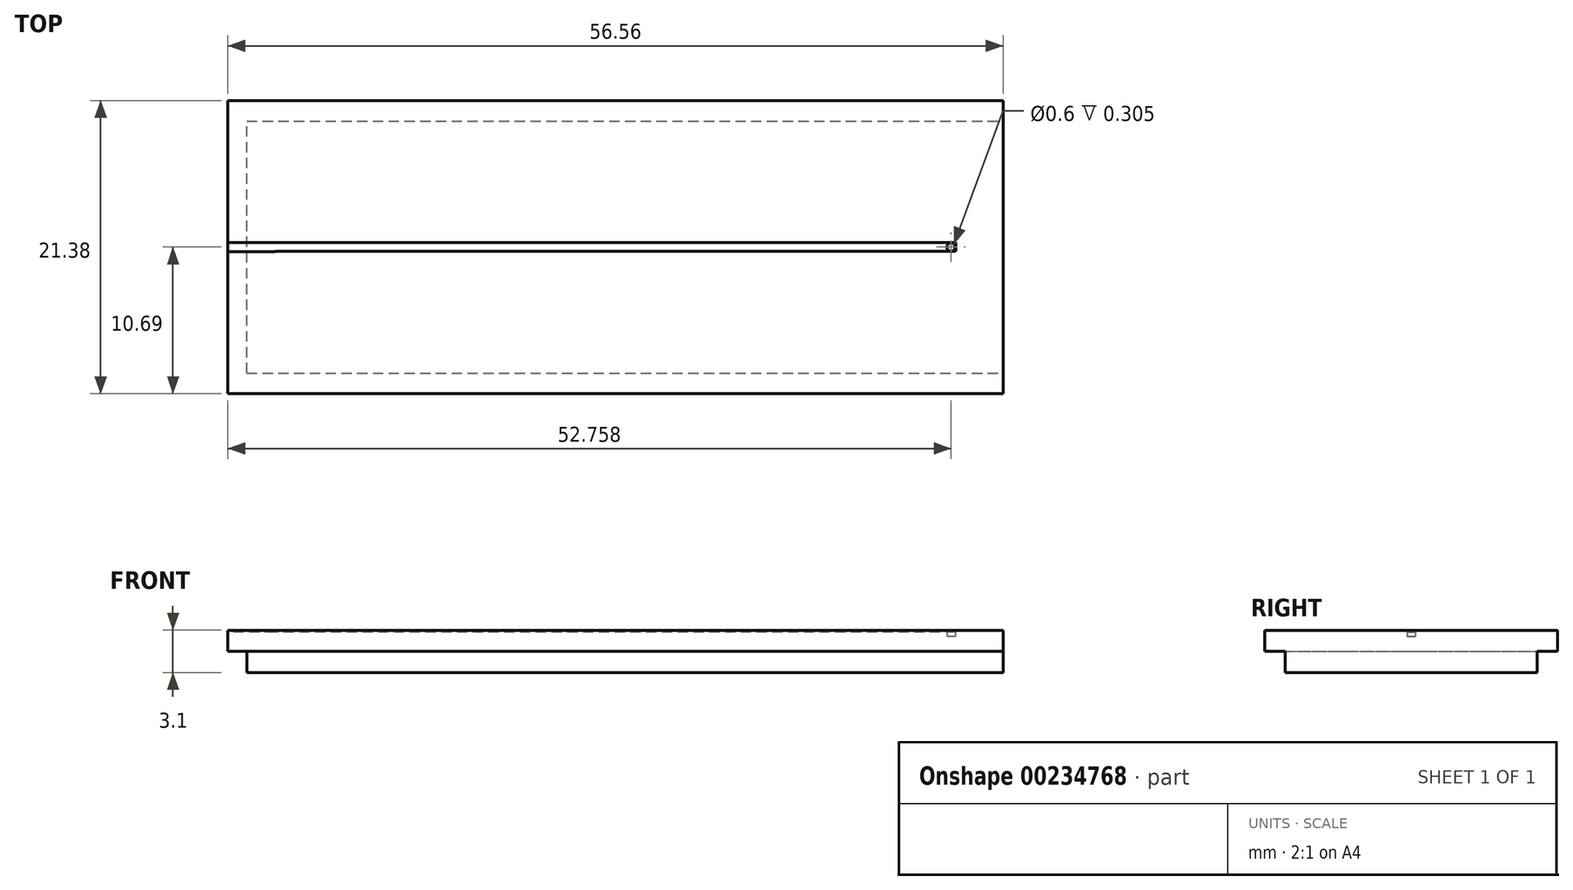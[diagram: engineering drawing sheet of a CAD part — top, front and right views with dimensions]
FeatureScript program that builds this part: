
annotation { "Feature Type Name" : "Feature", "Feature Type Description" : "" }
export const myFeature = defineFeature(function(context is Context, id is Id, definition is map)
    precondition{}
    {
        {
            var Q0;
            Q0=qCreatedBy(makeId("Top.planeOp"),FACE);
            var sketch = newSketch(context, id + "F5", { "sketchPlane" : qUnion([Q0])});
            skLineSegment(sketch, "E0.bottom", {"start": v(28.28, -10.69) * mm, "end": v(-28.28, -10.69) * mm});
            skLineSegment(sketch, "E0.top", {"start": v(28.28, 10.69) * mm, "end": v(-28.28, 10.69) * mm});
            skLineSegment(sketch, "E0.left", {"start": v(28.28, -10.69) * mm, "end": v(28.28, 10.69) * mm});
            skLineSegment(sketch, "E0.right", {"start": v(-28.28, -10.69) * mm, "end": v(-28.28, 10.69) * mm});
            skSolve(sketch);
        }
        {
            var Q0;
            Q0=makeQuery(id+"F5.imprint","IMPRINT",FACE,{"disambiguationData":[TD([[makeQuery(id+"F5.imprint","IMPRINT",EDGE,{"derivedFrom":sQuery(id+"F5.wireOp",EDGE,"E0.bottom")}),-1.0]])]});
            var sketch = newSketch(context, id + "F6", { "sketchPlane" : qUnion([Q0])});
            skCircle(sketch, "E1", {"center": v(24.48, 0) * mm, "radius": 0.3 * mm});
            skSolve(sketch);
        }
        {
            var Q0;
            Q0=makeQuery(id+"F6.imprint","IMPRINT",FACE,{"disambiguationData":[TD([[makeQuery(id+"F6.imprint","IMPRINT",EDGE,{"derivedFrom":sQuery(id+"F6.wireOp",EDGE,"E1")}),-1.0]])]});
            extrude(context, id + "F7", {"entities" : qUnion([Q0]), "depth" : 0.3 * mm});
        }
        {
            var Q0;
            Q0=makeQuery(id+"F7.opExtrude","CAP_FACE",FACE,{"disambiguationData":[OSD([sQuery(id+"F5.wireOp",EDGE,"E0.bottom"),sQuery(id+"F5.wireOp",EDGE,"E0.top"),sQuery(id+"F5.wireOp",EDGE,"E0.left"),sQuery(id+"F5.wireOp",EDGE,"E0.right"),sQuery(id+"F6.wireOp",EDGE,"E1")])],"isStart":false});
            var sketch = newSketch(context, id + "F0", { "sketchPlane" : qUnion([Q0])});
            skLineSegment(sketch, "E2.bottom", {"start": v(24.83, -0.32) * mm, "end": v(-24.83, -0.32) * mm});
            skLineSegment(sketch, "E2.top", {"start": v(24.83, 0.32) * mm, "end": v(-24.83, 0.32) * mm});
            skLineSegment(sketch, "E2.left", {"start": v(24.83, -0.32) * mm, "end": v(24.83, 0.32) * mm});
            skLineSegment(sketch, "E2.right", {"start": v(-24.83, -0.32) * mm, "end": v(-24.83, 0.32) * mm});
            skPoint(sketch, "E2.middle", {"position": v(0, 0) * mm});
            skSolve(sketch);
        }
        {
            var Q0;
            Q0=makeQuery(id+"F0.imprint","IMPRINT",FACE,{"disambiguationData":[TD([[makeQuery(id+"F0.imprint","IMPRINT",EDGE,{"derivedFrom":sQuery(id+"F0.wireOp",EDGE,"E2.bottom")}),1.0]])]});
            var sketch = newSketch(context, id + "F1", { "sketchPlane" : qUnion([Q0])});
            skLineSegment(sketch, "E3.bottom", {"start": v(-24.83, -0.32) * mm, "end": v(-28.28, -0.32) * mm});
            skLineSegment(sketch, "E3.top", {"start": v(-24.83, 0.32) * mm, "end": v(-28.28, 0.32) * mm});
            skLineSegment(sketch, "E3.left", {"start": v(-24.83, -0.32) * mm, "end": v(-24.83, 0.32) * mm});
            skLineSegment(sketch, "E3.right", {"start": v(-28.28, -0.32) * mm, "end": v(-28.28, 0.32) * mm});
            skSolve(sketch);
        }
        {
            var Q0;
            {var subQ1=makeQuery(id+"F0.imprint","IMPRINT",EDGE,{"derivedFrom":sQuery(id+"F0.wireOp",EDGE,"E2.top")});Q0=makeQuery(id+"F1.imprint","IMPRINT",FACE,{"disambiguationData":[TD([[makeQuery(id+"F1.imprint","IMPRINT",EDGE,{"derivedFrom":subQ1}),-1.0]])]});}
            extrude(context, id + "F8", {"entities" : qUnion([Q0]), "operationType" : NewBodyOperationType.ADD, "depth" : 0.15 * mm});
        }
        {
            var Q0;
            Q0=makeQuery(id+"F5.imprint","IMPRINT",FACE,{"disambiguationData":[TD([[makeQuery(id+"F5.imprint","IMPRINT",EDGE,{"derivedFrom":sQuery(id+"F5.wireOp",EDGE,"E0.bottom")}),-1.0]])]});
            extrude(context, id + "F9", {"entities" : qUnion([Q0]), "operationType" : NewBodyOperationType.ADD, "oppositeDirection" : true, "depth" : 1.1 * mm});
        }
        {
            var Q0;
            Q0=makeQuery(id+"F9.opExtrude","CAP_FACE",FACE,{"disambiguationData":[OSD([sQuery(id+"F5.wireOp",EDGE,"E0.bottom"),sQuery(id+"F5.wireOp",EDGE,"E0.top"),sQuery(id+"F5.wireOp",EDGE,"E0.left"),sQuery(id+"F5.wireOp",EDGE,"E0.right")])],"isStart":false});
            var sketch = newSketch(context, id + "F10", { "sketchPlane" : qUnion([Q0])});
            skLineSegment(sketch, "E4.bottom", {"start": v(-26.9, 10.69) * mm, "end": v(-28.28, 10.69) * mm});
            skLineSegment(sketch, "E4.top", {"start": v(-26.9, -10.69) * mm, "end": v(-28.28, -10.69) * mm});
            skLineSegment(sketch, "E4.left", {"start": v(-26.9, 10.69) * mm, "end": v(-26.9, -10.69) * mm});
            skLineSegment(sketch, "E4.right", {"start": v(-28.28, 10.69) * mm, "end": v(-28.28, -10.69) * mm});
            skSolve(sketch);
        }
        {
            var Q0;
            Q0=makeQuery(id+"F9.opExtrude","CAP_FACE",FACE,{"disambiguationData":[OSD([sQuery(id+"F5.wireOp",EDGE,"E0.bottom"),sQuery(id+"F5.wireOp",EDGE,"E0.top"),sQuery(id+"F5.wireOp",EDGE,"E0.left"),sQuery(id+"F5.wireOp",EDGE,"E0.right")])],"isStart":false});
            var sketch = newSketch(context, id + "F2", { "sketchPlane" : qUnion([Q0])});
            skLineSegment(sketch, "E5.bottom", {"start": v(-28.28, -9.18) * mm, "end": v(28.28, -9.18) * mm});
            skLineSegment(sketch, "E5.top", {"start": v(-28.28, -10.69) * mm, "end": v(28.28, -10.69) * mm});
            skLineSegment(sketch, "E5.left", {"start": v(-28.28, -9.18) * mm, "end": v(-28.28, -10.69) * mm});
            skLineSegment(sketch, "E5.right", {"start": v(28.28, -9.18) * mm, "end": v(28.28, -10.69) * mm});
            skSolve(sketch);
        }
        {
            var Q0;
            {var subQ5=makeQuery(id+"F9.opExtrude","CAP_EDGE",EDGE,{"disambiguationData":[OSD([sQuery(id+"F5.wireOp",EDGE,"E0.left")])],"isStart":false});Q0=makeQuery(id+"F10.imprint","IMPRINT",FACE,{"disambiguationData":[TD([[makeQuery(id+"F10.imprint","IMPRINT",EDGE,{"derivedFrom":subQ5}),-1.0]])]});}
            var sketch = newSketch(context, id + "F3", { "sketchPlane" : qUnion([Q0])});
            skLineSegment(sketch, "E6.bottom", {"start": v(-26.9, -9.18) * mm, "end": v(28.28, -9.18) * mm});
            skLineSegment(sketch, "E6.top", {"start": v(-26.9, 9.19) * mm, "end": v(28.28, 9.19) * mm});
            skLineSegment(sketch, "E6.left", {"start": v(-26.9, -9.18) * mm, "end": v(-26.9, 9.19) * mm});
            skLineSegment(sketch, "E6.right", {"start": v(28.28, -9.18) * mm, "end": v(28.28, 9.19) * mm});
            skSolve(sketch);
        }
        {
            var Q0;
            Q0=makeQuery(id+"F3.imprint","IMPRINT",FACE,{"disambiguationData":[TD([[makeQuery(id+"F3.imprint","IMPRINT",EDGE,{"derivedFrom":sQuery(id+"F3.wireOp",EDGE,"E6.bottom")}),1.0]])]});
            extrude(context, id + "F4", {"entities" : qUnion([Q0]), "operationType" : NewBodyOperationType.ADD, "depth" : 1.55 * mm});
        }
    });
